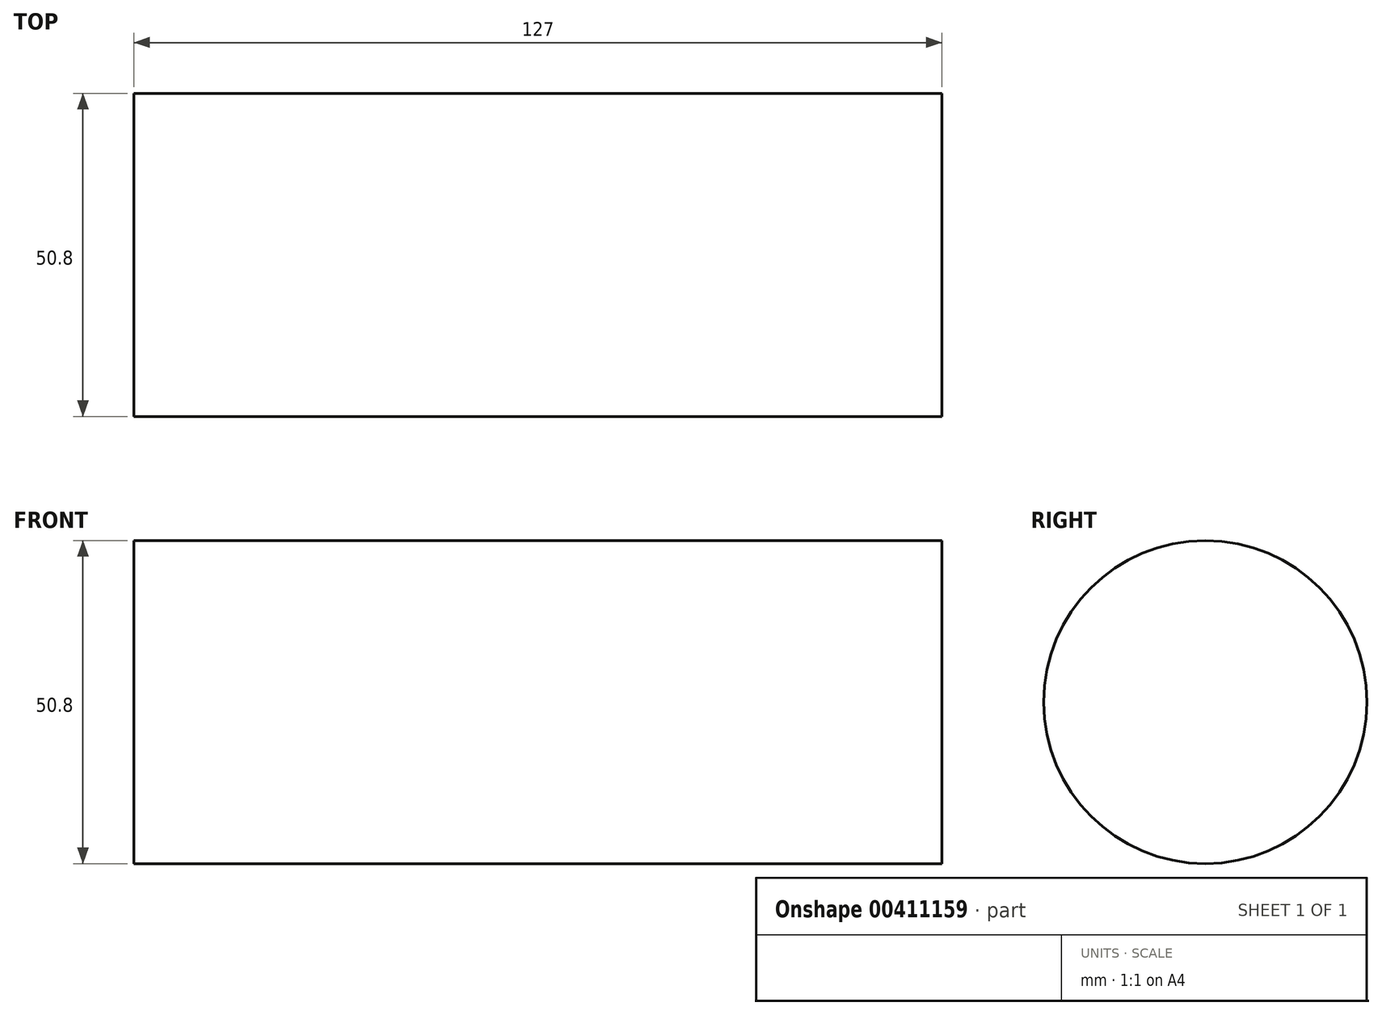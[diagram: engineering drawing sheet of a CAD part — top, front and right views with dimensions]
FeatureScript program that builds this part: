
annotation { "Feature Type Name" : "Feature", "Feature Type Description" : "" }
export const myFeature = defineFeature(function(context is Context, id is Id, definition is map)
    precondition{}
    {
        {
            var Q0;
            Q0=qCreatedBy(makeId("Right.planeOp"),FACE);
            var sketch = newSketch(context, id + "F0", { "sketchPlane" : qUnion([Q0])});
            skCircle(sketch, "E0", {"center": v(0, 0) * mm, "radius": 25.4 * mm});
            skSolve(sketch);
        }
        {
            var Q0;
            Q0 = qSketchRegion(id + "F0", true);
            extrude(context, id + "F1", {"entities" : qUnion([Q0]), "depth" : 127 * mm});
        }
    });
